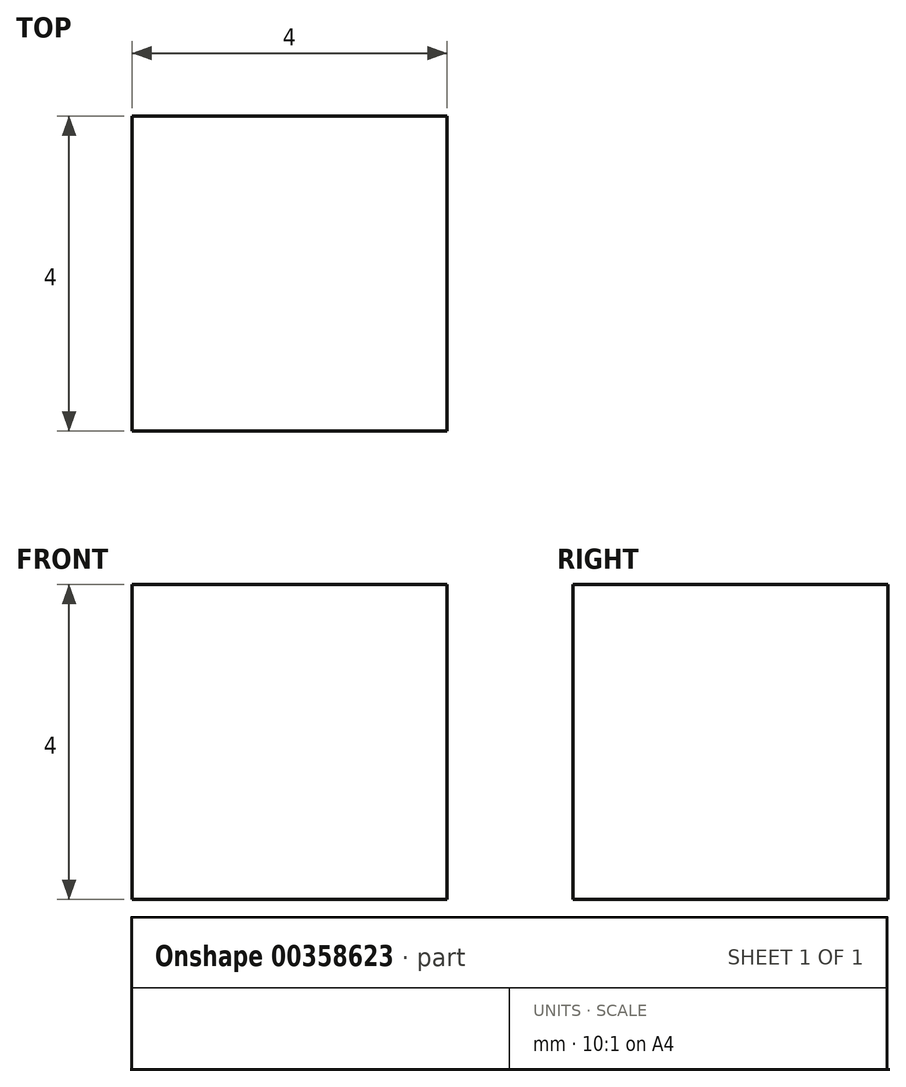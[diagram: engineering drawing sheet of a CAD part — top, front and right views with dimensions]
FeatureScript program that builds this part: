
annotation { "Feature Type Name" : "Feature", "Feature Type Description" : "" }
export const myFeature = defineFeature(function(context is Context, id is Id, definition is map)
    precondition{}
    {
        {
            var Q0;
            Q0=qCreatedBy(makeId("Front.planeOp"),FACE);
            var sketch = newSketch(context, id + "F0", { "sketchPlane" : qUnion([Q0])});
            skLineSegment(sketch, "E0.bottom", {"start": v(-2, 2) * mm, "end": v(2, 2) * mm});
            skLineSegment(sketch, "E0.top", {"start": v(-2, -2) * mm, "end": v(2, -2) * mm});
            skLineSegment(sketch, "E0.left", {"start": v(-2, 2) * mm, "end": v(-2, -2) * mm});
            skLineSegment(sketch, "E0.right", {"start": v(2, 2) * mm, "end": v(2, -2) * mm});
            skPoint(sketch, "E0.middle", {"position": v(0, 0) * mm});
            skSolve(sketch);
        }
        {
            var Q0;
            Q0 = qSketchRegion(id + "F0", true);
            extrude(context, id + "F1", {"entities" : qUnion([Q0]), "depth" : 4 * mm});
        }
    });
